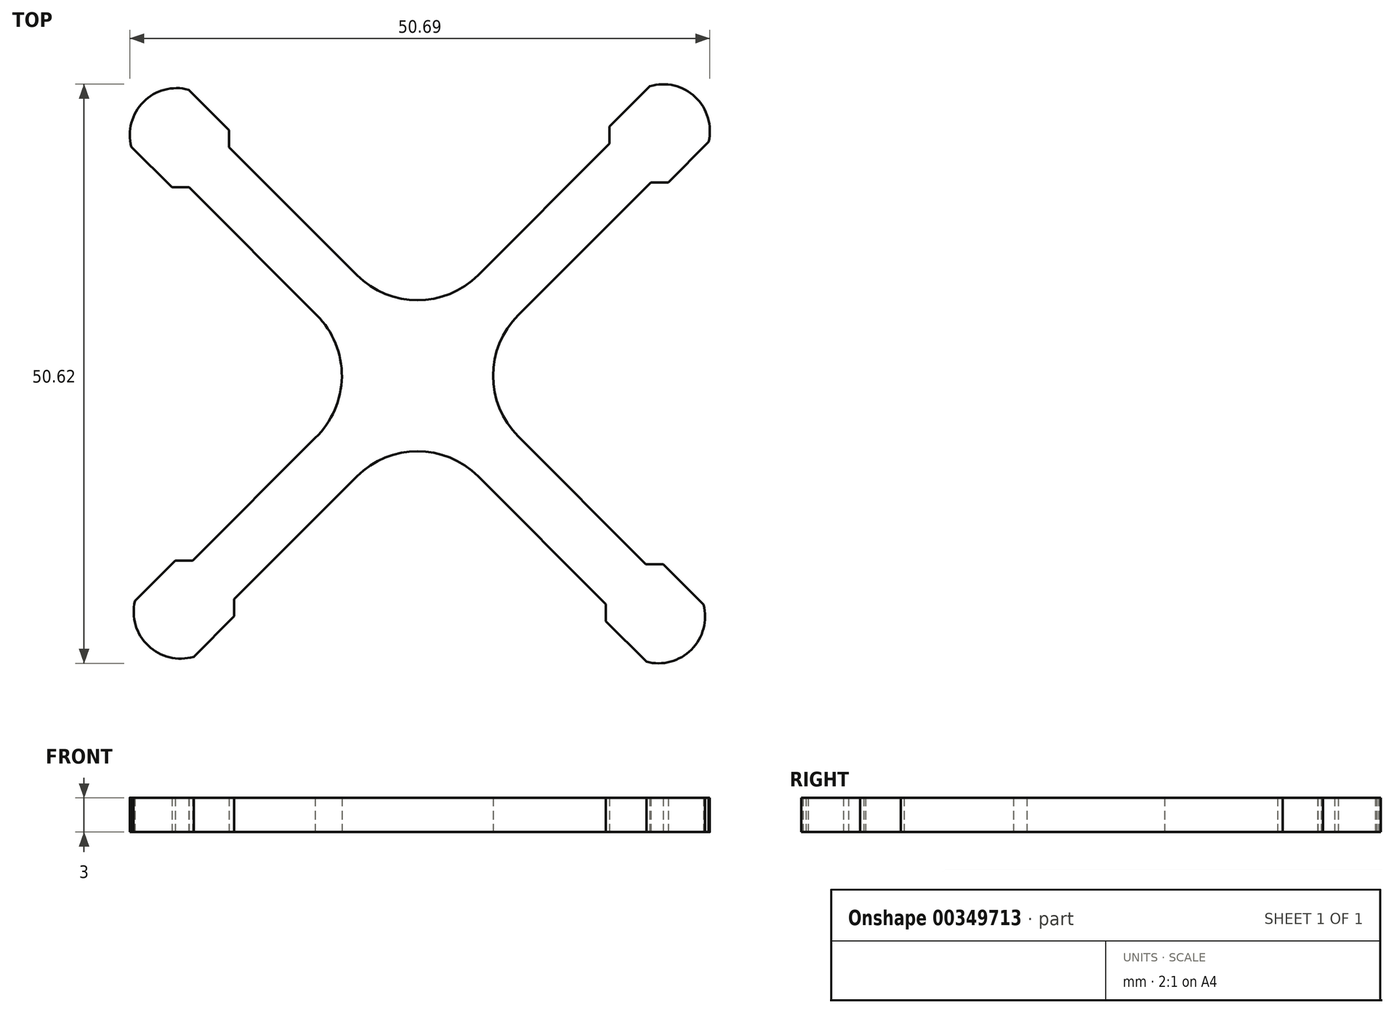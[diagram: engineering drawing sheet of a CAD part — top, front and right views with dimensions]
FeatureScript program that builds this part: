
annotation { "Feature Type Name" : "Feature", "Feature Type Description" : "" }
export const myFeature = defineFeature(function(context is Context, id is Id, definition is map)
    precondition{}
    {
        {
            var Q0;
            Q0=qCreatedBy(makeId("Top.planeOp"),FACE);
            var sketch = newSketch(context, id + "F0", { "sketchPlane" : qUnion([Q0])});
            skPoint(sketch, "E0.middle", {"position": v(0, 0) * mm});
            skLineSegment(sketch, "E1", {"start": v(-25, 20) * mm, "end": v(-21.46, 16.46) * mm});
            skLineSegment(sketch, "E2", {"start": v(-24.7, -19.7) * mm, "end": v(-21.16, -16.16) * mm});
            skLineSegment(sketch, "E3", {"start": v(20, -25) * mm, "end": v(16.46, -21.46) * mm});
            skLineSegment(sketch, "E4", {"start": v(25.44, 20.44) * mm, "end": v(21.9, 16.9) * mm});
            skLineSegment(sketch, "E5", {"start": v(-21.46, 16.46) * mm, "end": v(-19.96, 16.46) * mm});
            skLineSegment(sketch, "E6", {"start": v(-16.46, 21.46) * mm, "end": v(-16.46, 19.96) * mm});
            skLineSegment(sketch, "E7", {"start": v(16.77, 21.77) * mm, "end": v(16.77, 20.27) * mm});
            skLineSegment(sketch, "E8", {"start": v(21.9, 16.9) * mm, "end": v(20.4, 16.9) * mm});
            skLineSegment(sketch, "E9", {"start": v(21.46, -16.46) * mm, "end": v(19.96, -16.46) * mm});
            skLineSegment(sketch, "E10", {"start": v(16.46, -21.46) * mm, "end": v(16.46, -19.96) * mm});
            skLineSegment(sketch, "E11", {"start": v(-21.16, -16.16) * mm, "end": v(-19.66, -16.16) * mm});
            skLineSegment(sketch, "E12", {"start": v(-16.02, -21.02) * mm, "end": v(-16.02, -19.52) * mm});
            skLineSegment(sketch, "E13", {"start": v(21.46, -16.46) * mm, "end": v(25, -20) * mm});
            skLineSegment(sketch, "E14", {"start": v(-16.02, -21.02) * mm, "end": v(-19.56, -24.56) * mm});
            skLineSegment(sketch, "E15", {"start": v(-20, 25) * mm, "end": v(-16.46, 21.46) * mm});
            skLineSegment(sketch, "E16", {"start": v(20.3, 25.3) * mm, "end": v(16.77, 21.77) * mm});
            skArc(sketch, "E17", {"start": v(-20, 25) * mm, "mid": v(-23.94, 23.94) * mm, "end": v(-25, 20) * mm});
            skArc(sketch, "E18", {"start": v(20, -25) * mm, "mid": v(23.94, -23.94) * mm, "end": v(25, -20) * mm});
            skArc(sketch, "E19", {"start": v(-24.7, -19.7) * mm, "mid": v(-23.53, -23.6) * mm, "end": v(-19.56, -24.56) * mm});
            skArc(sketch, "E20", {"start": v(25.44, 20.44) * mm, "mid": v(24.28, 24.35) * mm, "end": v(20.3, 25.3) * mm});
            skLineSegment(sketch, "E21", {"start": v(-16.02, -19.52) * mm, "end": v(-5.3, -8.8) * mm});
            skLineSegment(sketch, "E22", {"start": v(-19.66, -16.16) * mm, "end": v(-8.94, -5.44) * mm});
            skArc(sketch, "E23", {"start": v(8.8, 5.3) * mm, "mid": v(6.6, 0) * mm, "end": v(8.8, -5.3) * mm});
            skArc(sketch, "E24", {"start": v(-5.3, 8.8) * mm, "mid": v(0, 6.6) * mm, "end": v(5.3, 8.8) * mm});
            skArc(sketch, "E25", {"start": v(-8.94, -5.44) * mm, "mid": v(-6.6, -0.1) * mm, "end": v(-8.8, 5.3) * mm});
            skArc(sketch, "E26", {"start": v(5.3, -8.8) * mm, "mid": v(0, -6.6) * mm, "end": v(-5.3, -8.8) * mm});
            skLineSegment(sketch, "E27", {"start": v(-19.96, 16.46) * mm, "end": v(-8.8, 5.3) * mm});
            skLineSegment(sketch, "E28", {"start": v(-16.46, 19.96) * mm, "end": v(-5.3, 8.8) * mm});
            skLineSegment(sketch, "E29", {"start": v(5.3, 8.8) * mm, "end": v(16.77, 20.27) * mm});
            skLineSegment(sketch, "E30", {"start": v(8.8, 5.3) * mm, "end": v(20.4, 16.9) * mm});
            skLineSegment(sketch, "E31", {"start": v(8.8, -5.3) * mm, "end": v(19.96, -16.46) * mm});
            skLineSegment(sketch, "E32", {"start": v(5.3, -8.8) * mm, "end": v(16.46, -19.96) * mm});
            skLineSegment(sketch, "E33.bottom", {"start": v(3, -3) * mm, "end": v(-3, -3) * mm});
            skLineSegment(sketch, "E33.top", {"start": v(3, 3) * mm, "end": v(-3, 3) * mm});
            skLineSegment(sketch, "E33.left", {"start": v(3, -3) * mm, "end": v(3, 3) * mm});
            skLineSegment(sketch, "E33.right", {"start": v(-3, -3) * mm, "end": v(-3, 3) * mm});
            skSolve(sketch);
        }
        {
            var Q0;
            Q0=qSketchRegion(id+"F0",true);
            var Q1;
            Q1=makeQuery(id+"F0.imprint","IMPRINT",FACE,{"disambiguationData":[TD([[makeQuery(id+"F0.imprint","IMPRINT",EDGE,{"derivedFrom":sQuery(id+"F0.wireOp",EDGE,"E33.bottom")}),-1.0]])]});
            extrude(context, id + "F1", {"entities" : qUnion([Q0, Q1]), "depth" : 3 * mm});
        }
    });
